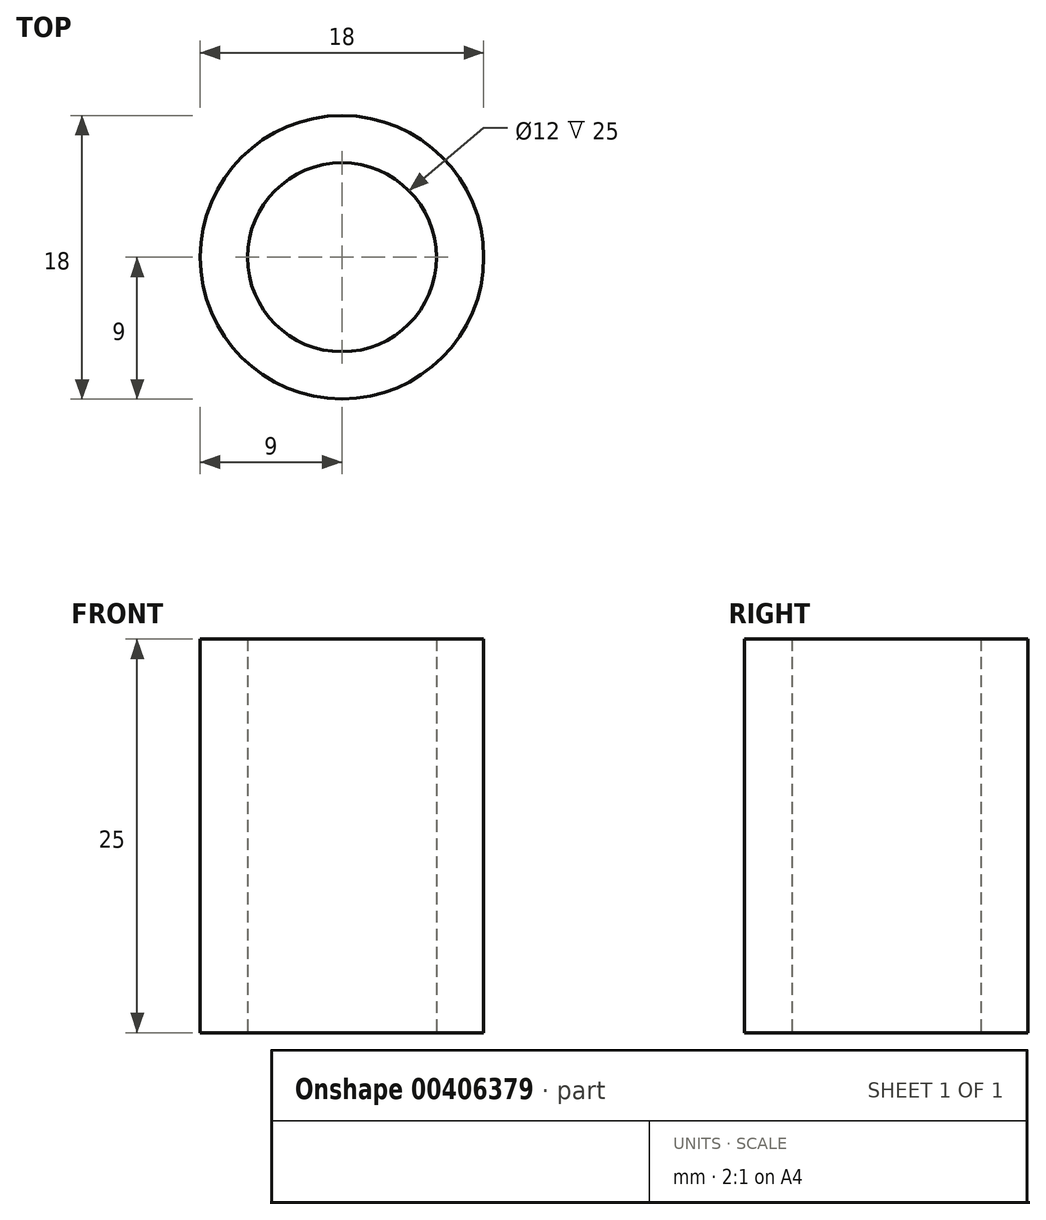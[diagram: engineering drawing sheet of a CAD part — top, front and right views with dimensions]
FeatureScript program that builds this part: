
annotation { "Feature Type Name" : "Feature", "Feature Type Description" : "" }
export const myFeature = defineFeature(function(context is Context, id is Id, definition is map)
    precondition{}
    {
        {
            var Q0;
            Q0=qCreatedBy(makeId("Top.planeOp"),FACE);
            var sketch = newSketch(context, id + "F0", { "sketchPlane" : qUnion([Q0])});
            skCircle(sketch, "E0", {"center": v(0, 0) * mm, "radius": 9 * mm});
            skCircle(sketch, "E1", {"center": v(0, 0) * mm, "radius": 6 * mm});
            skSolve(sketch);
        }
        {
            var Q0;
            Q0=makeQuery(id+"F0.imprint","IMPRINT",FACE,{"disambiguationData":[TD([[makeQuery(id+"F0.imprint","IMPRINT",EDGE,{"derivedFrom":sQuery(id+"F0.wireOp",EDGE,"E0")}),1.0]])]});
            extrude(context, id + "F1", {"entities" : qUnion([Q0]), "depth" : 25 * mm});
        }
    });
